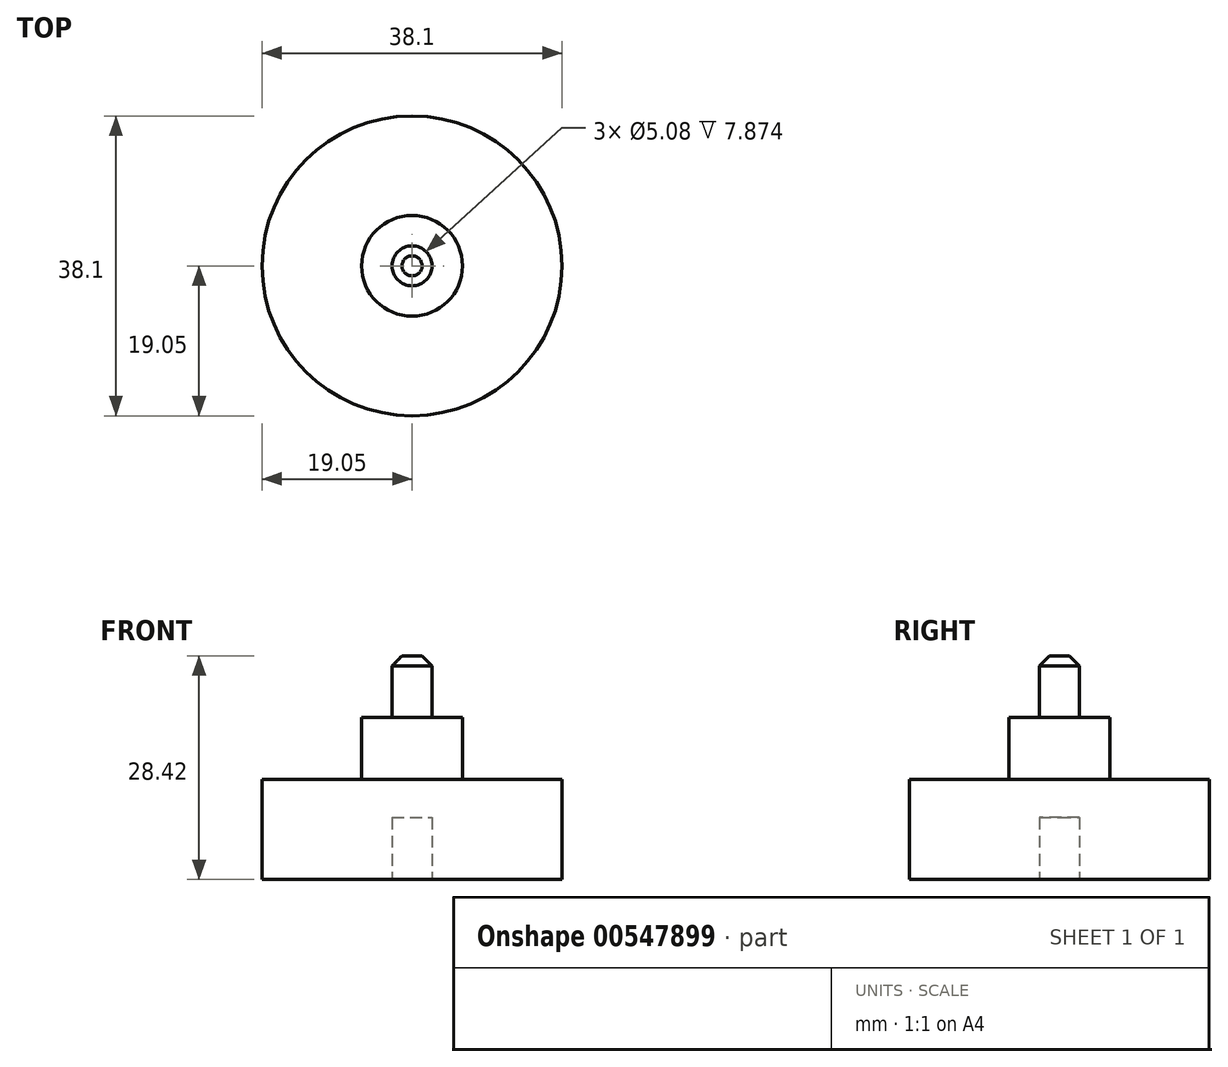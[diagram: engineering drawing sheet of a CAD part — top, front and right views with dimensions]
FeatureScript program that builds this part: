
annotation { "Feature Type Name" : "Feature", "Feature Type Description" : "" }
export const myFeature = defineFeature(function(context is Context, id is Id, definition is map)
    precondition{}
    {
        {
            var Q0;
            Q0=qCreatedBy(makeId("Front.planeOp"),FACE);
            var sketch = newSketch(context, id + "F0", { "sketchPlane" : qUnion([Q0])});
            skLineSegment(sketch, "E0", {"start": v(0, 0) * mm, "end": v(19.05, 0) * mm});
            skLineSegment(sketch, "E1", {"start": v(19.05, 0) * mm, "end": v(19.05, 12.7) * mm});
            skLineSegment(sketch, "E2", {"start": v(19.05, 12.7) * mm, "end": v(6.4, 12.7) * mm});
            skLineSegment(sketch, "E3", {"start": v(2.54, 20.57) * mm, "end": v(6.4, 20.57) * mm});
            skLineSegment(sketch, "E4", {"start": v(6.4, 20.57) * mm, "end": v(6.4, 12.7) * mm});
            skLineSegment(sketch, "E5", {"start": v(0, 28.42) * mm, "end": v(2.54, 28.42) * mm});
            skLineSegment(sketch, "E6", {"start": v(2.54, 28.42) * mm, "end": v(2.54, 20.57) * mm});
            skPoint(sketch, "E7.start.orphan", {"position": v(0, 12.7) * mm});
            skLineSegment(sketch, "E8", {"start": v(0, 0) * mm, "end": v(2.54, 0) * mm});
            skLineSegment(sketch, "E9", {"start": v(2.54, 0) * mm, "end": v(2.54, 7.87) * mm});
            skLineSegment(sketch, "E10", {"start": v(2.54, 7.87) * mm, "end": v(0, 7.87) * mm});
            skLineSegment(sketch, "E11", {"start": v(0, 7.87) * mm, "end": v(0, 28.42) * mm});
            skSolve(sketch);
        }
        {
            var Q0;
            Q0 = qSketchRegion(id + "F0", true);
            var Q1;
            Q1=sQuery(id+"F0.wireOp",EDGE,"E11");
            revolve(context, id + "F1", {"entities" : qUnion([Q0]), "axis" : qUnion([Q1]), "revolveType" : RevolveType.FULL});
        }
        {
            var Q0;
            Q0=makeQuery(id+"F1.opRevolve","SWEPT_EDGE",EDGE,{"disambiguationData":[OSD([sQuery(id+"F0.wireOp",EDGE,"E5"),sQuery(id+"F0.wireOp",EDGE,"E6")])]});
            chamfer(context, id + "F2", {"entities" : qUnion([Q0]), "width" : 1.27 * mm, "tangentPropagation" : true});
        }
    });
